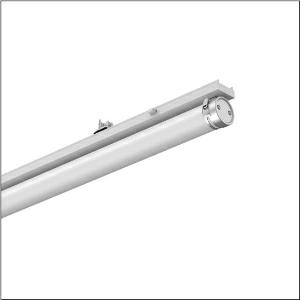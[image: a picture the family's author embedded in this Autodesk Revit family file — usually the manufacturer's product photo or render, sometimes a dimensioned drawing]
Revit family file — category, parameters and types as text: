
# Revit family: monsun_r__31_tube_51ft10mn4a0atr1_8ef5
name_source: partatom
category: Lighting Fixtures
units: mm (PartAtom-declared; Revit-internal decimal feet)

## family parameters
Cut with Voids When Loaded = No
Host = Face
Light Source = No
Part Type = Normal
Room Calculation Point = No
Round Connector Dimension = Use Diameter
Shared = No

## types (1)
- --- (1 x LED, 10000 lm, 58 W, 4000K)
    Apparent Load = 58 VA
    CIE Flux Codes = 42 71 90 91 100
    Color Rendering = 80
    Color Temperature = 4000K
    Default Elevation = 1800 mm
    Description = Monsun® 31 Tube, tubular luminaire, primary optical cover: diffuser, of PMMA, light emission: direct distribution, primary light characteristic: symmetric, LED, rated luminous flux: 10.000lm, luminous efficacy: 172lm/W, light colour: 840, colour temperature: 4000K, with with 1 terminal, 3-pole, max. 2.5mm², mains connection: 220..240V, AC, 50/60Hz, rated input power: 58W, housing, cylindrical, of PMMA, semi-transparent, matt white, with luminaire and ceiling fastening, V4A, mounting with brackets of stainless steel, length: 1.495mm, diameter: 75mm, end cap, of stainless steel (V4A), protection rating (complete): IP20, protection rating (lamp compartment): IP67/69K, insulation class (complete): insulation class I (protective earthing), certification: CE, UKCA, impact resistance: IK07, permissible operating ambient temperature: -20..+40°C, corresponds to IFS (International Featured Standards) requirements for safety and quality in the food industry, contact your sales advisor before using the luminaires in applications with unclear chemical exposure, large temperature fluctuations or condensation-forming humidity, packaging unit: 1 piece
    Height = 118 mm
    Lamp = 1 x LED
    Lamp Light Flux = 10000 lm
    Lamp Power = 58 W
    Lamp count = 1
    Length = 1495 mm
    Luminous efficacy = 172 lm/W
    Manufacturer = Siteco
    ModVariant = No
    Model = 51FT10MN4A0ATR1
    Mounting Place = Ceiling
    Mounting Type = Pendant
    Number of Poles = 1
    OnlyDefault = Yes
    Power Factor = 1
    Product Name = Monsun® 31 Tube
    Product group = tubular luminaire
    ProductGroupID = 906
    Protection Class = Protection class I
    Protection Degree = IP 20
    RLX_Detail_Level = 1
    RLX_Emergency_Light_Flux = 0 lm
    RLX_Emergency_Type = 0
    RLX_Emergency_Type_DB = No
    RlxData = <blob elided: 32269 chars, md5=016f1e71>
    Socket = socket
    Standby Power = 0 W
    System Light Flux = 10000 lm
    System Power = 58 W
    Type Comments = factory setting: luminous flux: 100 % | (OFF | OFF | OFF | OFF) | 350 mA
    Type Image = l_1007227.jpg
    URL = http://relux.com
    VarID = @adj_074703
    Voltage = 0 V
    Weight = 0.00 kg
    Width = 75 mm

## geometry (parser evidence)
native form markers: Blend x4, Sweep x12
no freeform markers — native parametric forms only
